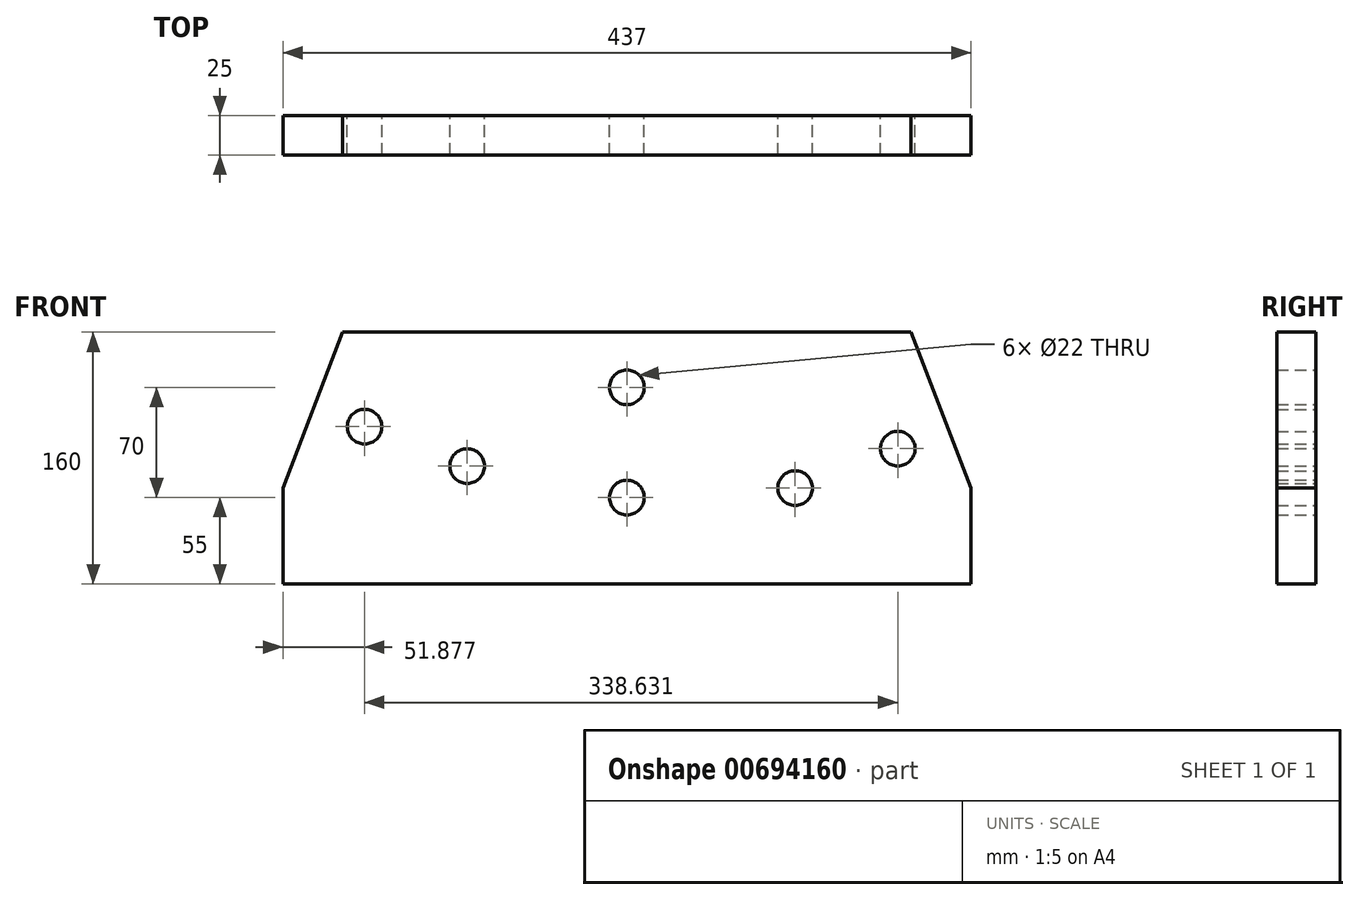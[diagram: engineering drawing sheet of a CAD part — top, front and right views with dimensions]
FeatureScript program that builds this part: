
annotation { "Feature Type Name" : "Feature", "Feature Type Description" : "" }
export const myFeature = defineFeature(function(context is Context, id is Id, definition is map)
    precondition{}
    {
        {
            var Q0;
            Q0=qCreatedBy(makeId("Front.planeOp"),FACE);
            var sketch = newSketch(context, id + "F0", { "sketchPlane" : qUnion([Q0])});
            skLineSegment(sketch, "E0", {"start": v(-218.5, 0) * mm, "end": v(218.5, 0) * mm});
            skLineSegment(sketch, "E1", {"start": v(218.5, 0) * mm, "end": v(218.5, 61) * mm});
            skLineSegment(sketch, "E2", {"start": v(218.5, 61) * mm, "end": v(180.5, 160) * mm});
            skLineSegment(sketch, "E3", {"start": v(180.5, 160) * mm, "end": v(-180.5, 160) * mm});
            skLineSegment(sketch, "E4", {"start": v(-180.5, 160) * mm, "end": v(-218.5, 61) * mm});
            skLineSegment(sketch, "E5", {"start": v(-218.5, 61) * mm, "end": v(-218.5, 0) * mm});
            skLineSegment(sketch, "E6", {"start": v(0, 0) * mm, "end": v(0, 160) * mm, "construction": true});
            skCircle(sketch, "E7", {"center": v(-166.62, 100) * mm, "radius": 11 * mm});
            skCircle(sketch, "E8", {"center": v(-101.5, 75) * mm, "radius": 11 * mm});
            skCircle(sketch, "E9", {"center": v(0, 125) * mm, "radius": 11 * mm});
            skCircle(sketch, "E10", {"center": v(0, 55) * mm, "radius": 11 * mm});
            skCircle(sketch, "E11", {"center": v(106.88, 61) * mm, "radius": 11 * mm});
            skCircle(sketch, "E12", {"center": v(172, 86) * mm, "radius": 11 * mm});
            skLineSegment(sketch, "E13", {"start": v(106.88, 61) * mm, "end": v(204.17, 98.34) * mm, "construction": true});
            skLineSegment(sketch, "E14", {"start": v(-101.5, 75) * mm, "end": v(-198.8, 112.35) * mm, "construction": true});
            skSolve(sketch);
        }
        {
            var Q0;
            Q0=makeQuery(id+"F0.imprint","IMPRINT",FACE,{"disambiguationData":[TD([[makeQuery(id+"F0.imprint","IMPRINT",EDGE,{"derivedFrom":sQuery(id+"F0.wireOp",EDGE,"E0")}),1.0]])]});
            extrude(context, id + "F1", {"entities" : qUnion([Q0]), "depth" : 25 * mm, "offsetDistance" : 25 * mm});
        }
    });
